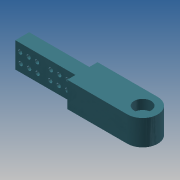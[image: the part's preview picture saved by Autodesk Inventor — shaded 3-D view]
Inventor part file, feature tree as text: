
AUTODESK INVENTOR PART (.ipt)
format: ipt  version: 2013 (Build 170138000, 138)  size: 181,760 bytes
history: native  units: mm
features: extrude x8, sketch x8, fillet x1
ambient origin geometry x8: Origin, YZ Plane, XZ Plane, XY Plane, X Axis, Y Axis, Z Axis, Center Point
bodies: Solid1 (feature_tree)
feature tree (17):
  extrude  "Extrusion1"  Depth=12.6mm
  extrude  "Extrusion2"  Depth=8.5mm
  extrude  "Extrusion3"  Depth=22.0mm
  extrude  "Extrusion4"  Depth=20.0mm
  extrude  "Extrusion5"  Depth=7.0mm TaperAngle=0.0deg
  fillet  "Fillet1"  Radius=3.0mm
  extrude  "Extrusion7"  Depth=35.0mm
  extrude  "Extrusion8"  Depth=6.0mm
  extrude  "Extrusion9"  Depth=50.0mm
  sketch  "Sketch1"  dims[d0=150.0mm d2=12.6mm]
  sketch  "Sketch2"  dims[d3=15.0mm d4=8.5mm]
  sketch  "Sketch4"  dims[d5=21.1mm d6=0.0mm d7=22.0mm]
  sketch  "Sketch5"  dims[d9=7.0mm d10=0.0mm d16=20.0mm]
  sketch  "Sketch6"  dims[d17=40.0mm d18=7.0mm d19=0.0mm d21=3.0mm d22=0.0mm]
  sketch  "Sketch8"  dims[d23=3.5mm d24=35.0mm]
  sketch  "Sketch9"  dims[d26=10.0mm d27=0.0mm d28=6.0mm]
  sketch  "Sketch10"  dims[d34=3.5mm d35=50.0mm d36=50.0mm d37=11.5mm d38=10.0mm d39=0.0mm d40=12.5mm d41=8.0mm d42=0.5mm d43=1.0mm d44=1.5mm d45=2.0mm d46=2.5mm d47=3.5mm d48=25.0mm d49=0.5mm d50=1.0mm d51=1.5mm d52=2.0mm d53=2.5mm d54=10.0mm d55=0.0mm d56=13.0mm d57=8.0mm d58=0.0mm]
